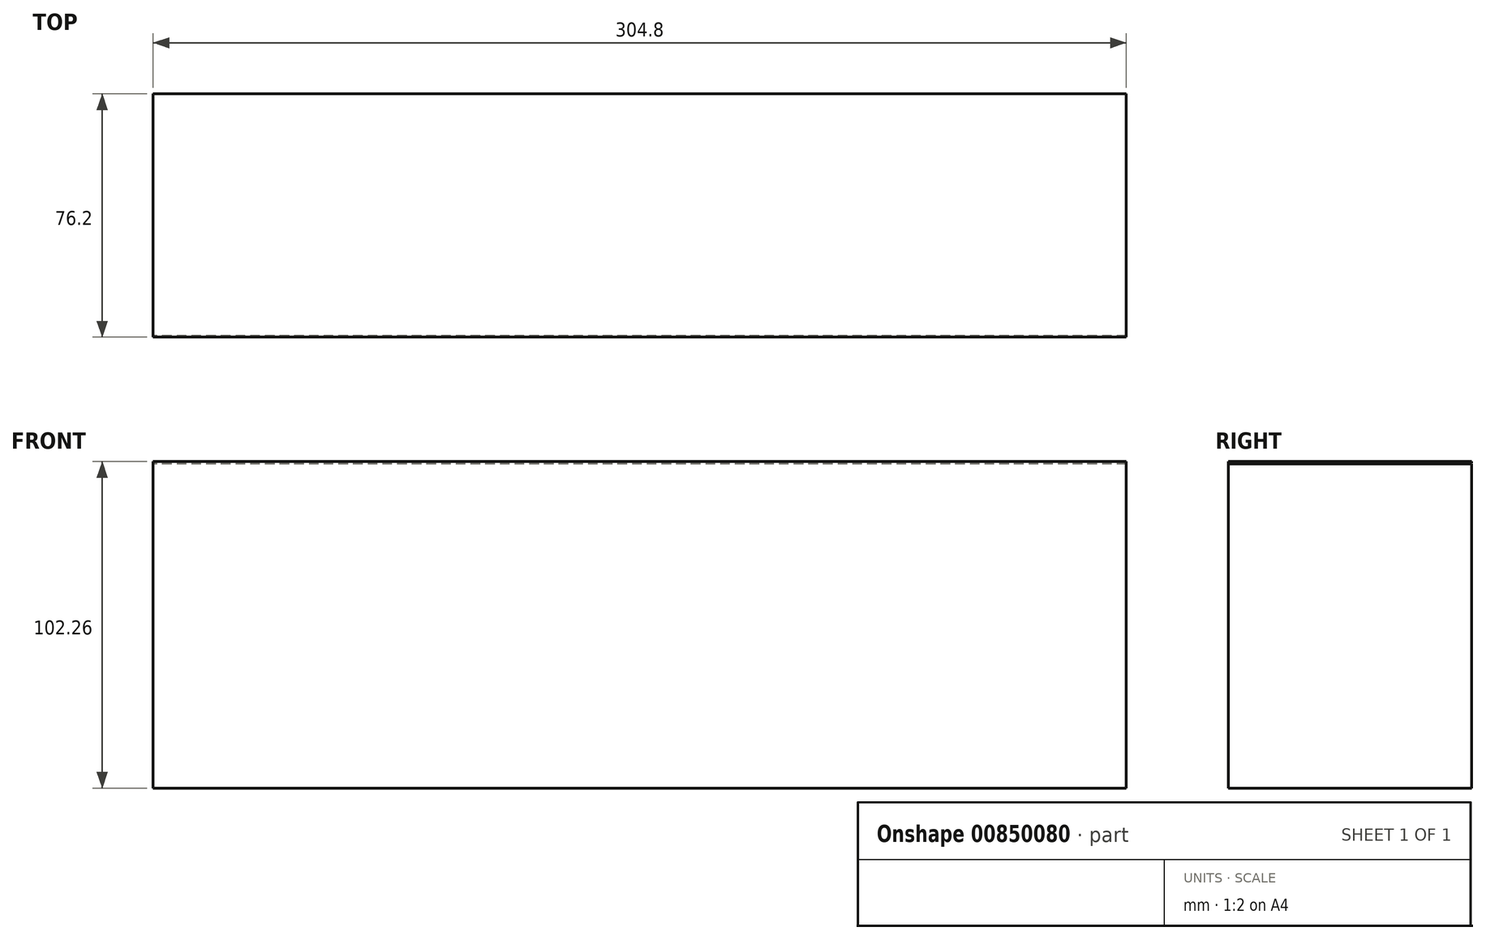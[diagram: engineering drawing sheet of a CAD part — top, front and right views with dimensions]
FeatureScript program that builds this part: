
annotation { "Feature Type Name" : "Feature", "Feature Type Description" : "" }
export const myFeature = defineFeature(function(context is Context, id is Id, definition is map)
    precondition{}
    {
        {
            var Q0;
            Q0=qCreatedBy(makeId("Right.planeOp"),FACE);
            var sketch = newSketch(context, id + "F0", { "sketchPlane" : qUnion([Q0])});
            skLineSegment(sketch, "E0.bottom", {"start": v(0, 0) * mm, "end": v(-76.2, 0) * mm});
            skLineSegment(sketch, "E0.top", {"start": v(0, 101.6) * mm, "end": v(-75.8, 101.6) * mm});
            skLineSegment(sketch, "E0.left", {"start": v(0, 0) * mm, "end": v(0, 101.6) * mm});
            skLineSegment(sketch, "E0.right", {"start": v(-76.2, 0) * mm, "end": v(-76.2, 102.26) * mm});
            skLineSegment(sketch, "E1", {"start": v(-76.2, 102.26) * mm, "end": v(0, 102.26) * mm});
            skLineSegment(sketch, "E2", {"start": v(0, 102.26) * mm, "end": v(0, 101.85) * mm});
            skLineSegment(sketch, "E3", {"start": v(0, 101.85) * mm, "end": v(-75.8, 101.85) * mm});
            skLineSegment(sketch, "E4", {"start": v(-75.8, 101.6) * mm, "end": v(-75.8, 101.85) * mm});
            skLineSegment(sketch, "E5", {"start": v(-75.8, 101.6) * mm, "end": v(-76.2, 101.6) * mm, "construction": true});
            skSolve(sketch);
        }
        {
            var Q0;
            Q0=qSketchRegion(id+"F0",true);
            extrude(context, id + "F1", {"entities" : qUnion([Q0]), "endBound" : BoundingType.SYMMETRIC, "depth" : 304.8 * mm, "offsetDistance" : 25.4 * mm});
        }
    });
